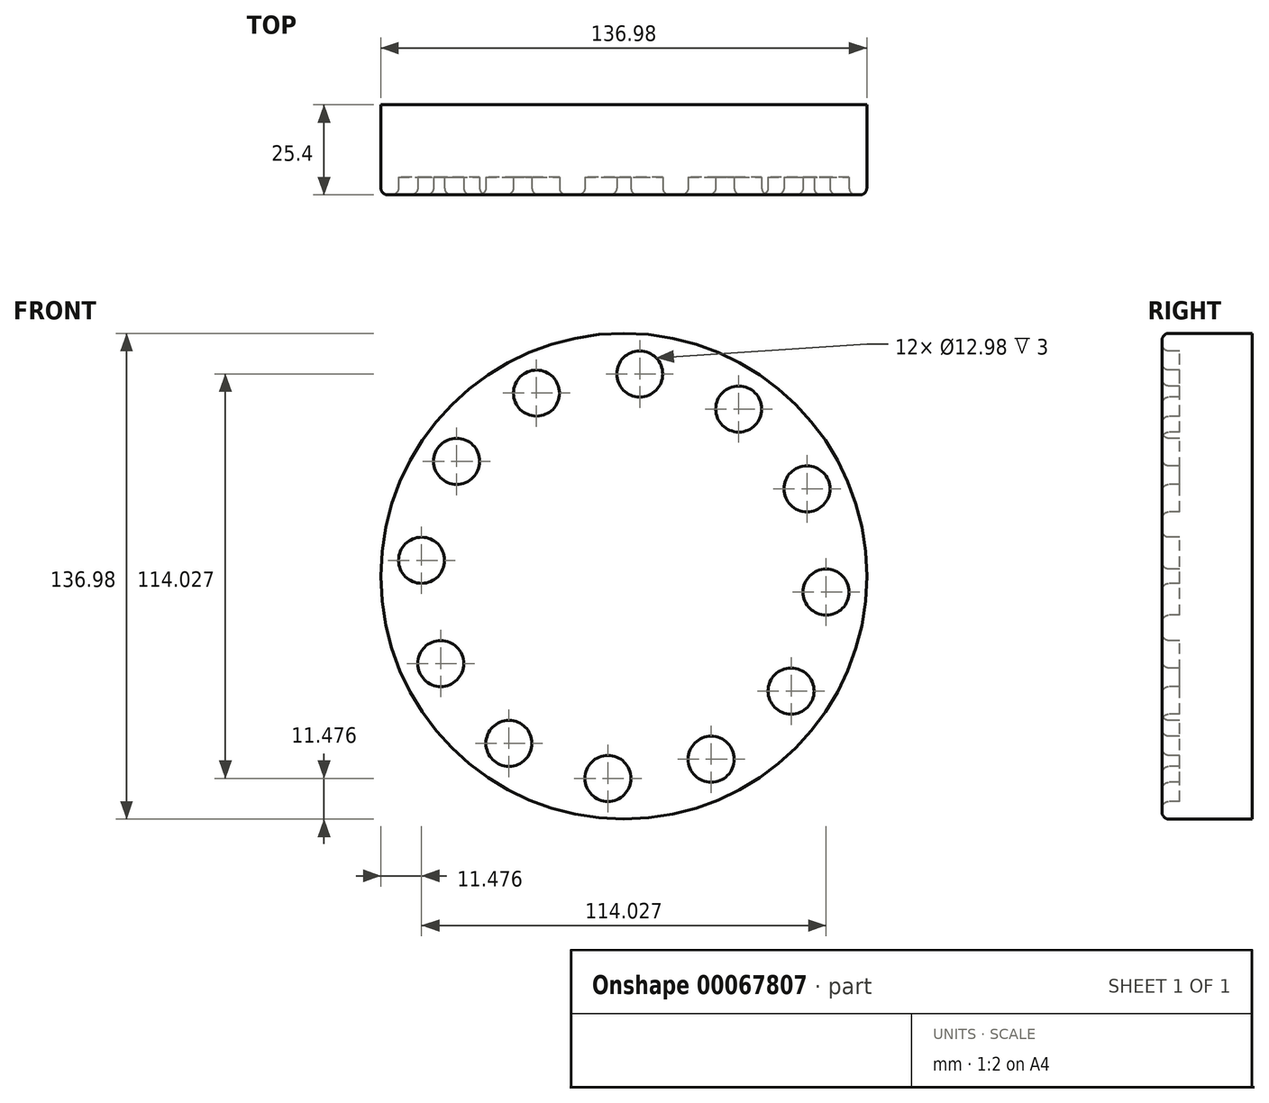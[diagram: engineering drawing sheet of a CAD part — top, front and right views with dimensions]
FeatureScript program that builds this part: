
annotation { "Feature Type Name" : "Feature", "Feature Type Description" : "" }
export const myFeature = defineFeature(function(context is Context, id is Id, definition is map)
    precondition{}
    {
        {
            var Q0;
            Q0=qCreatedBy(makeId("Front.planeOp"),FACE);
            var sketch = newSketch(context, id + "F0", { "sketchPlane" : qUnion([Q0])});
            skCircle(sketch, "E0", {"center": v(-4.48, 0) * mm, "radius": 68.49 * mm});
            skSolve(sketch);
        }
        {
            var Q0;
            Q0 = qSketchRegion(id + "F0", true);
            extrude(context, id + "F1", {"entities" : qUnion([Q0]), "depth" : 25.4 * mm});
        }
        {
            var Q0;
            Q0=makeQuery(id+"F1.opExtrude","CAP_FACE",FACE,{"disambiguationData":[OSD([sQuery(id+"F0.wireOp",EDGE,"E0")])],"isStart":false});
            var sketch = newSketch(context, id + "F2", { "sketchPlane" : qUnion([Q0])});
            skCircle(sketch, "E1", {"center": v(0, 57.01) * mm, "radius": 6.49 * mm});
            skCircle(sketch, "E2.1.0", {"center": v(-29.1, 51.62) * mm, "radius": 6.49 * mm});
            skCircle(sketch, "E2.2.0", {"center": v(-51.62, 32.39) * mm, "radius": 6.49 * mm});
            skCircle(sketch, "E2.3.0", {"center": v(-61.5, 4.48) * mm, "radius": 6.49 * mm});
            skCircle(sketch, "E2.4.0", {"center": v(-56.1, -24.63) * mm, "radius": 6.49 * mm});
            skCircle(sketch, "E2.5.0", {"center": v(-36.87, -47.14) * mm, "radius": 6.49 * mm});
            skCircle(sketch, "E2.6.0", {"center": v(-8.96, -57.01) * mm, "radius": 6.49 * mm});
            skCircle(sketch, "E2.7.0", {"center": v(20.15, -51.62) * mm, "radius": 6.49 * mm});
            skCircle(sketch, "E2.8.0", {"center": v(42.66, -32.39) * mm, "radius": 6.49 * mm});
            skCircle(sketch, "E2.9.0", {"center": v(52.53, -4.48) * mm, "radius": 6.49 * mm});
            skCircle(sketch, "E2.10.0", {"center": v(47.14, 24.63) * mm, "radius": 6.49 * mm});
            skCircle(sketch, "E2.11.0", {"center": v(27.9, 47.14) * mm, "radius": 6.49 * mm});
            skPoint(sketch, "E2.center", {"position": v(-4.48, 0) * mm});
            skSolve(sketch);
        }
        {
            var Q0;
            Q0 = qSketchRegion(id + "F2", true);
            extrude(context, id + "F3", {"entities" : qUnion([Q0]), "operationType" : NewBodyOperationType.REMOVE, "oppositeDirection" : true, "depth" : 5 * mm});
        }
        {
            var Q0;
            Q0=makeQuery(id+"F1.opExtrude","CAP_FACE",FACE,{"disambiguationData":[OSD([sQuery(id+"F0.wireOp",EDGE,"E0")])],"isStart":false});
            fillet(context, id + "F4", {"entities" : qUnion([Q0]), "radius" : 2 * mm, "tangentPropagation" : true, "allowEdgeOverflow" : false});
        }
    });
